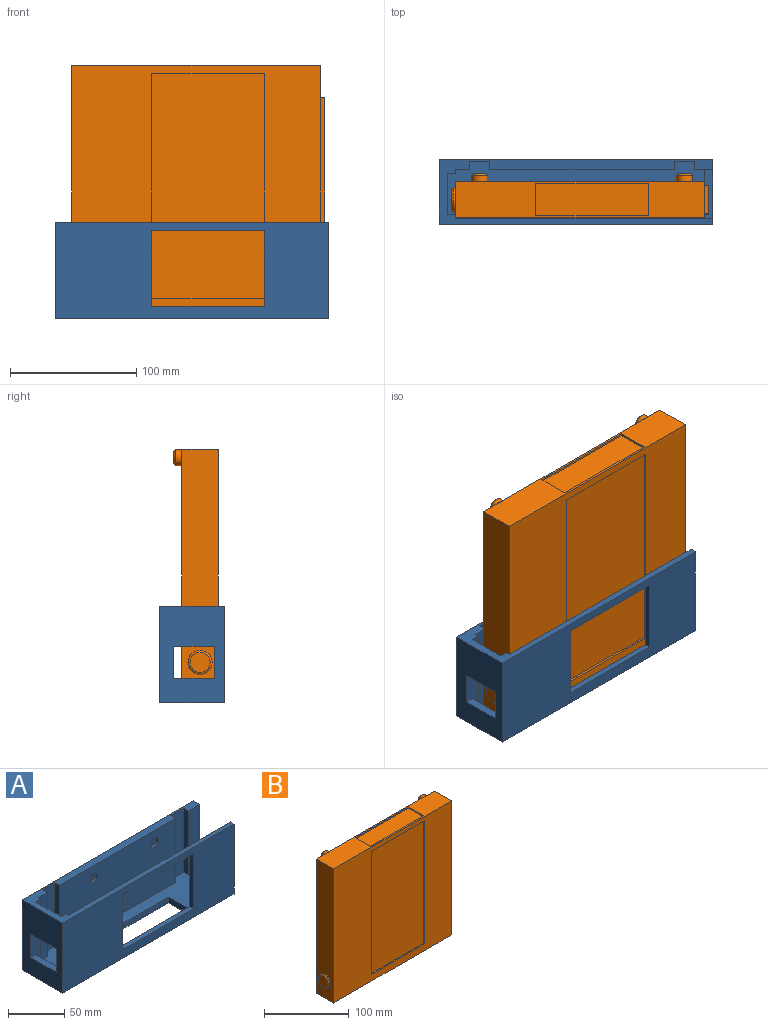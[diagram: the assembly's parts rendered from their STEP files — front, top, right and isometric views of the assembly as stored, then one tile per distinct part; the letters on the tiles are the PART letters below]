
ASSEMBLY  parts=2 mates=1
PART A: 41 faces, bbox 215.9x50.8x76.2 mm
  f0: plane 38.1x12.7mm, normal (-1,0,0), area 483.9mm2, adj f2,f12,f14,f34
  f1: plane 76.2x50.8mm, normal (1,0,0), area 1693.5mm2, adj f3,f5,f10,f11,f12,f14,f34
  f2: plane 203.2x44.45mm, normal (0,0,1), area 5645.1mm2, adj f0,f4,f6,f7,f8,f12,f13,f14
  f3: plane 215.9x50.8mm, normal (0,0,-1), area 8709.7mm2, adj f1,f9,f10,f11,f26,f27,f28,f29
  f4: plane 31.75x12.7mm, normal (1,0,0), area 403.2mm2, adj f2,f16,f17,f24
  f5: plane 215.9x50.8mm, normal (0,0,1), area 2822.6mm2, adj f1,f6,f7,f8,f9,f10,f11,f12
  f6: plane 69.85x11.11mm, normal (0,-1,0), area 776.2mm2, adj f2,f5,f8,f20
  f7: plane 146.05x69.85mm, normal (0,-1,0), area 10049.9mm2, adj f2,f5,f19,f23,f35,f37
  f8: plane 69.85x3.18mm, normal (1,0,0), area 221.8mm2, adj f2,f5,f6,f17
  f9: plane 76.2x50.8mm, normal (-1,0,0), area 3064.5mm2, adj f3,f5,f10,f11,f16,f17,f24,f25
  f10: plane 215.9x76.2mm, normal (0,-1,0), area 11138.1mm2, adj f1,f3,f5,f9,f30,f31,f32,f33
  f11: plane 215.9x76.2mm, normal (0,1,0), area 16416mm2, adj f1,f3,f5,f9,f39,f40
  f12: plane 69.85x14.29mm, normal (0,-1,0), area 917.3mm2, adj f0,f1,f2,f5,f21,f34
  f13: plane 69.85x3.18mm, normal (1,0,0), area 221.8mm2, adj f2,f5,f14,f16
  f14: plane 203.2x69.85mm, normal (0,1,0), area 8799.4mm2, adj f0,f1,f2,f5,f13,f30,f31,f32
  f15: plane 31.75x31.75mm, normal (1,0,0), area 1008.1mm2, adj f5,f16,f17,f25
  f16: plane 69.85x12.7mm, normal (0,1,0), area 604.8mm2, adj f2,f4,f5,f9,f13,f15,f24,f25
  f17: plane 69.85x12.7mm, normal (0,-1,0), area 604.8mm2, adj f2,f4,f5,f8,f9,f15,f24,f25
  f18: plane 69.85x15.88mm, normal (0,-1,0), area 1108.9mm2, adj f2,f5,f19,f20
  f19: plane 69.85x6.35mm, normal (-1,0,0), area 443.5mm2, adj f2,f5,f7,f18
  f20: plane 69.85x6.35mm, normal (1,0,0), area 443.5mm2, adj f2,f5,f6,f18
  f21: plane 69.85x6.35mm, normal (-1,0,0), area 443.5mm2, adj f2,f5,f12,f22
  f22: plane 69.85x15.88mm, normal (0,-1,0), area 1108.9mm2, adj f2,f5,f21,f23
  f23: plane 69.85x6.35mm, normal (1,0,0), area 443.5mm2, adj f2,f5,f7,f22
  f24: plane 31.75x6.35mm, normal (0,0,1), area 201.6mm2, adj f4,f9,f16,f17
  f25: plane 31.75x6.35mm, normal (0,0,-1), area 201.6mm2, adj f9,f15,f16,f17
  f26: plane 88.9x6.35mm, normal (0,1,0), area 564.5mm2, adj f2,f3,f27,f29
  f27: plane 25.4x6.35mm, normal (1,0,0), area 161.3mm2, adj f2,f3,f26,f28
  f28: plane 88.9x6.35mm, normal (0,-1,0), area 564.5mm2, adj f2,f3,f27,f29
  f29: plane 25.4x6.35mm, normal (-1,0,0), area 161.3mm2, adj f2,f3,f26,f28
  f30: plane 88.9x4.76mm, normal (0,0,1), area 423.4mm2, adj f10,f14,f31,f32
  f31: plane 59.77x4.76mm, normal (1,0,0), area 284.7mm2, adj f10,f14,f30,f33
  f32: plane 59.77x4.76mm, normal (-1,0,0), area 284.7mm2, adj f10,f14,f30,f33
  f33: plane 88.9x4.76mm, normal (0,0,-1), area 423.4mm2, adj f10,f14,f31,f32
  f34: plane 38.1x6.35mm, normal (0,0,1), area 241.9mm2, adj f0,f1,f12,f14
  f35: cylinder r=5.06mm len=10.12mm, axis (0,-1,0), area 101mm2, adj f7,f36
  f36: plane 10.12x10.12mm, normal (0,-1,0), area 62.7mm2, adj f35,f40
  f37: cylinder r=4.76mm len=9.53mm, axis (0,-1,0), area 95mm2, adj f7,f38
  f38: plane 9.53x9.53mm, normal (0,-1,0), area 53.4mm2, adj f37,f39
  f39: cylinder r=2.38mm len=4.76mm, axis (0,-1,0), area 71.3mm2, adj f11,f38
  f40: cylinder r=2.38mm len=4.76mm, axis (0,-1,0), area 71.3mm2, adj f11,f36
PART B: 49 faces, bbox 203.2x34.9x193.7 mm
  f0: plane 193.68x28.58mm, normal (1,0,0), area 2147.2mm2, adj f1,f2,f3,f5,f44,f45,f46,f47
  f1: plane 196.85x28.58mm, normal (0,0,-1), area 3366.9mm2, adj f0,f2,f4,f5,f14,f15,f16,f17
  f2: plane 196.85x193.68mm, normal (0,-1,0), area 22318.5mm2, adj f0,f1,f3,f4,f9,f10,f11,f12
  f3: plane 196.85x28.58mm, normal (0,0,1), area 3366.9mm2, adj f0,f2,f4,f5,f19,f20,f21,f22
  f4: plane 193.68x28.58mm, normal (-1,0,0), area 5249.2mm2, adj f1,f2,f3,f5,f6
  f5: plane 196.85x193.68mm, normal (0,1,0), area 37618.2mm2, adj f0,f1,f3,f4,f24,f26,f28,f30
  f6: cylinder r=9.53mm len=19.05mm, axis (1,0,0), area 95mm2, adj f4,f8
  f7: plane 15.88x15.88mm, normal (-1,0,0), area 197.9mm2, adj f8
  f8: torus R=7.94mm, axis (-1,0,0), area 140.2mm2, adj f6,f7
  f9: plane 88.9x1.59mm, normal (0,0,-1), area 141.1mm2, adj f2,f10,f12,f13
  f10: plane 177.8x1.59mm, normal (1,0,0), area 282.3mm2, adj f2,f9,f11,f13
  f11: plane 88.9x1.59mm, normal (0,0,1), area 141.1mm2, adj f2,f10,f12,f13
  f12: plane 177.8x1.59mm, normal (-1,0,0), area 282.3mm2, adj f2,f9,f11,f13
  f13: plane 177.8x88.9mm, normal (0,-1,0), area 15806.4mm2, adj f9,f10,f11,f12
  f14: plane 88.9x1.59mm, normal (0,1,0), area 141.1mm2, adj f1,f15,f17,f18
  f15: plane 25.4x1.59mm, normal (1,0,0), area 40.3mm2, adj f1,f14,f16,f18
  f16: plane 88.9x1.59mm, normal (0,-1,0), area 141.1mm2, adj f1,f15,f17,f18
  f17: plane 25.4x1.59mm, normal (-1,0,0), area 40.3mm2, adj f1,f14,f16,f18
  f18: plane 88.9x25.4mm, normal (0,0,-1), area 2258.1mm2, adj f14,f15,f16,f17
  f19: plane 88.9x1.59mm, normal (0,1,0), area 141.1mm2, adj f3,f20,f22,f23
  f20: plane 25.4x1.59mm, normal (-1,0,0), area 40.3mm2, adj f3,f19,f21,f23
  f21: plane 88.9x1.59mm, normal (0,-1,0), area 141.1mm2, adj f3,f20,f22,f23
  f22: plane 25.4x1.59mm, normal (1,0,0), area 40.3mm2, adj f3,f19,f21,f23
  f23: plane 88.9x25.4mm, normal (0,0,1), area 2258.1mm2, adj f19,f20,f21,f22
  f24: cylinder r=6.35mm len=12.7mm, axis (0,-1,0), area 190mm2, adj f5,f35
  f25: plane 9.53x9.53mm, normal (0,1,0), area 39.6mm2, adj f35,f42
  f26: cylinder r=6.35mm len=12.7mm, axis (0,-1,0), area 190mm2, adj f5,f32
  f27: plane 9.53x9.53mm, normal (0,1,0), area 39.6mm2, adj f32,f40
  f28: cylinder r=6.35mm len=12.7mm, axis (0,-1,0), area 190mm2, adj f5,f33
  f29: plane 9.53x9.53mm, normal (0,1,0), area 39.6mm2, adj f33,f38
  f30: cylinder r=6.35mm len=12.7mm, axis (0,-1,0), area 190mm2, adj f5,f34
  f31: plane 9.53x9.53mm, normal (0,1,0), area 39.6mm2, adj f34,f36
  f32: cone r=4.76mm half-angle=45deg, axis (0,-1,0), area 78.4mm2, adj f26,f27
  f33: cone r=4.76mm half-angle=45deg, axis (0,-1,0), area 78.4mm2, adj f28,f29
  f34: cone r=4.76mm half-angle=45deg, axis (0,-1,0), area 78.4mm2, adj f30,f31
  f35: cone r=4.76mm half-angle=45deg, axis (0,-1,0), area 78.4mm2, adj f24,f25
  f36: cylinder r=3.17mm len=6.35mm, axis (0,1,0), area 95mm2, adj f31,f37
  f37: plane 6.35x6.35mm, normal (0,1,0), area 31.7mm2, adj f36
  f38: cylinder r=3.17mm len=6.35mm, axis (0,1,0), area 95mm2, adj f29,f39
  f39: plane 6.35x6.35mm, normal (0,1,0), area 31.7mm2, adj f38
  f40: cylinder r=3.17mm len=6.35mm, axis (0,1,0), area 95mm2, adj f27,f41
  f41: plane 6.35x6.35mm, normal (0,1,0), area 31.7mm2, adj f40
  f42: cylinder r=3.17mm len=6.35mm, axis (0,1,0), area 95mm2, adj f25,f43
  f43: plane 6.35x6.35mm, normal (0,1,0), area 31.7mm2, adj f42
  f44: plane 152.4x3.18mm, normal (0,-1,0), area 483.9mm2, adj f0,f45,f47,f48
  f45: plane 22.23x3.18mm, normal (0,0,-1), area 70.6mm2, adj f0,f44,f46,f48
  f46: plane 152.4x3.18mm, normal (0,1,0), area 483.9mm2, adj f0,f45,f47,f48
  f47: plane 22.23x3.18mm, normal (0,0,1), area 70.6mm2, adj f0,f44,f46,f48
  f48: plane 152.4x22.23mm, normal (1,0,0), area 3387.1mm2, adj f44,f45,f46,f47
PLACE A t=(-122.48,24.75,36.44)mm
PLACE B t=(-11.36,7.29,139.63)mm
MATE fastened B.f1 <-> A.f2  axis (0,0,-1) through (-109.78,-21.29,42.79)mm
